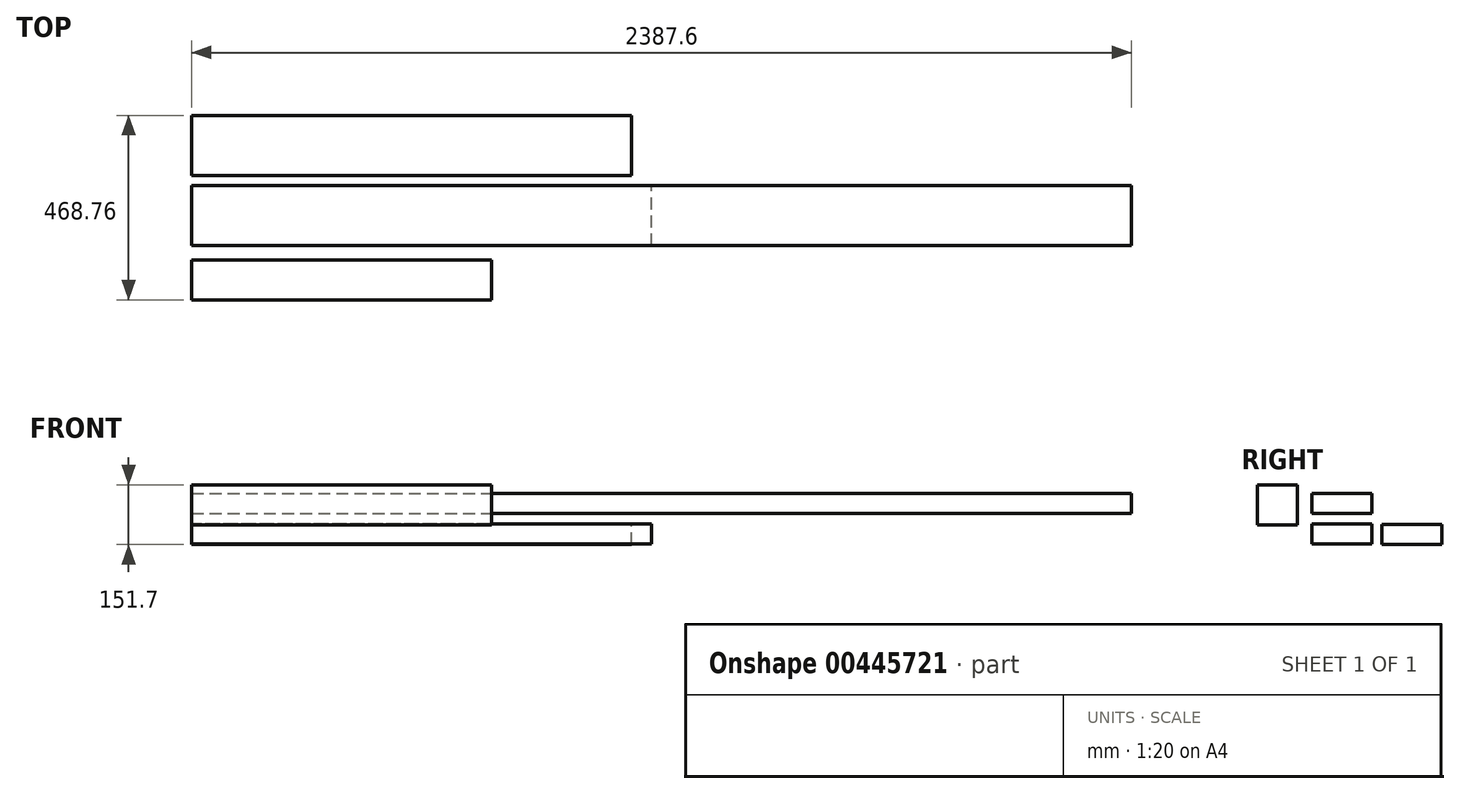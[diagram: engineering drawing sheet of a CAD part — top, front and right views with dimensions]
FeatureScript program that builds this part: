
annotation { "Feature Type Name" : "Feature", "Feature Type Description" : "" }
export const myFeature = defineFeature(function(context is Context, id is Id, definition is map)
    precondition{}
    {
        {
            var Q0;
            Q0=qCreatedBy(makeId("Top.planeOp"),FACE);
            var sketch = newSketch(context, id + "F0", { "sketchPlane" : qUnion([Q0])});
            skLineSegment(sketch, "E0.bottom", {"start": v(0, 0) * mm, "end": v(2387.6, 0) * mm});
            skLineSegment(sketch, "E0.top", {"start": v(0, 152.4) * mm, "end": v(2387.6, 152.4) * mm});
            skLineSegment(sketch, "E0.left", {"start": v(0, 0) * mm, "end": v(0, 152.4) * mm});
            skLineSegment(sketch, "E0.right", {"start": v(2387.6, 0) * mm, "end": v(2387.6, 152.4) * mm});
            skSolve(sketch);
        }
        {
            var Q0;
            Q0=makeQuery(id+"F0.imprint","IMPRINT",FACE,{"disambiguationData":[TD([[makeQuery(id+"F0.imprint","IMPRINT",EDGE,{"derivedFrom":sQuery(id+"F0.wireOp",EDGE,"E0.bottom")}),1.0]])]});
            extrude(context, id + "F1", {"entities" : qUnion([Q0]), "depth" : 50.8 * mm});
        }
        {
            var Q0;
            Q0=qCreatedBy(makeId("Right.planeOp"),FACE);
            var sketch = newSketch(context, id + "F2", { "sketchPlane" : qUnion([Q0])});
            skLineSegment(sketch, "E1.bottom", {"start": v(-36.44, -29.52) * mm, "end": v(-138.04, -29.52) * mm});
            skLineSegment(sketch, "E1.top", {"start": v(-36.44, 72.08) * mm, "end": v(-138.04, 72.08) * mm});
            skLineSegment(sketch, "E1.left", {"start": v(-36.44, -29.52) * mm, "end": v(-36.44, 72.08) * mm});
            skLineSegment(sketch, "E1.right", {"start": v(-138.04, -29.52) * mm, "end": v(-138.04, 72.08) * mm});
            skSolve(sketch);
        }
        {
            var Q0;
            Q0=makeQuery(id+"F2.imprint","IMPRINT",FACE,{"disambiguationData":[TD([[makeQuery(id+"F2.imprint","IMPRINT",EDGE,{"derivedFrom":sQuery(id+"F2.wireOp",EDGE,"E1.bottom")}),-1.0]])]});
            extrude(context, id + "F3", {"entities" : qUnion([Q0]), "depth" : 762 * mm});
        }
        {
            var Q0;
            Q0=qCreatedBy(makeId("Right.planeOp"),FACE);
            var sketch = newSketch(context, id + "F4", { "sketchPlane" : qUnion([Q0])});
            skLineSegment(sketch, "E2.bottom", {"start": v(0, -27.49) * mm, "end": v(152.4, -27.49) * mm});
            skLineSegment(sketch, "E2.top", {"start": v(0, -78.29) * mm, "end": v(152.4, -78.29) * mm});
            skLineSegment(sketch, "E2.left", {"start": v(0, -27.49) * mm, "end": v(0, -78.29) * mm});
            skLineSegment(sketch, "E2.right", {"start": v(152.4, -27.49) * mm, "end": v(152.4, -78.29) * mm});
            skSolve(sketch);
        }
        {
            var Q0;
            Q0=makeQuery(id+"F4.imprint","IMPRINT",FACE,{"disambiguationData":[TD([[makeQuery(id+"F4.imprint","IMPRINT",EDGE,{"derivedFrom":sQuery(id+"F4.wireOp",EDGE,"E2.bottom")}),-1.0]])]});
            extrude(context, id + "F5", {"entities" : qUnion([Q0]), "depth" : 1168.4 * mm});
        }
        {
            var Q0;
            Q0=qCreatedBy(makeId("Right.planeOp"),FACE);
            var sketch = newSketch(context, id + "F6", { "sketchPlane" : qUnion([Q0])});
            skLineSegment(sketch, "E3.bottom", {"start": v(178.32, -79.62) * mm, "end": v(330.72, -79.62) * mm});
            skLineSegment(sketch, "E3.top", {"start": v(178.32, -28.82) * mm, "end": v(330.72, -28.82) * mm});
            skLineSegment(sketch, "E3.left", {"start": v(178.32, -79.62) * mm, "end": v(178.32, -28.82) * mm});
            skLineSegment(sketch, "E3.right", {"start": v(330.72, -79.62) * mm, "end": v(330.72, -28.82) * mm});
            skSolve(sketch);
        }
        {
            var Q0;
            Q0=makeQuery(id+"F6.imprint","IMPRINT",FACE,{"disambiguationData":[TD([[makeQuery(id+"F6.imprint","IMPRINT",EDGE,{"derivedFrom":sQuery(id+"F6.wireOp",EDGE,"E3.bottom")}),1.0]])]});
            extrude(context, id + "F7", {"entities" : qUnion([Q0]), "depth" : 1117.6 * mm});
        }
    });
